# Revit family: Shower-Showerhead_Handshower_Set-KOHLER-Deluxe-K-26914_1
name_source: partatom
category: Plumbing Fixtures
units: mm (PartAtom-declared; Revit-internal decimal feet)

## family parameters
Cut with Voids When Loaded = No
Host = Face
Maintain Annotation Orientation = No
OmniClass Number = 23.31.17.00
OmniClass Title = Showers
Part Type = Normal
Room Calculation Point = No
Round Connector Dimension = Use Diameter
Shared = No

## types (6) — shared parameters
ADA Compliant = No
Assembly Code = D2010700
CW Connection = No
Cold Water Inlet = Cold Water Inlet
Date Modified = 06/23/2022
Default Elevation = 42"
Drain Included = No
HW Connection = Yes
Height = 24 1/4"
Hot Water Inlet = Tempered Water Inlet1
Length = 14 5/8"
Manufacturer = Kohler Co.
Master Format 2014 = 22 42 23
Master Format 2014 Name = Residential Showers
Material = Premium Metal Construction
Pressure = 80.00 psi
Product Documentation Link = https://www.us.kohler.com
Product Name = Deluxe
Product Page URL = http://www.us.kohler.com
Tempered Water Inlet2 = Tempered Water Inlet2
URL = https://www.us.kohler.com
Vent Connection = No
Waste Connection = No
Waste Water Outlet = Waste Water Outlet
WaterSense Certified = No
Width = 7 7/8"

## per-type parameters (varying)
| type | Description | Finish | Flow Rate | Model | Secondary Material | Type |
| 1.75 GPM, CP-Polished Chrome | Shower Kit 1.75 GPM | Kohler-Metal-CP-Polished_Chrome | 2 GPM | K-26914-G-CP | Kohler-Plastic-0-White | 1 |
| 1.75 GPM, BL-Matte Black | Shower Kit 1.75 GPM | Kohler-Metal-BL-Matte_Black | 2 GPM | K-26914-G-BL | Kohler-Plastic-58-Thunder_Grey | 2 |
| 1.75 GPM, 2MB-Vibrant Brushed Moderne Brass | Shower Kit 1.75 GPM | Kohler-Metal-2MB-Vibrant_Brushed_Moderne_Brass | 2 GPM | K-26914-G-2MB | Kohler-Plastic-0-White | 3 |
| 2.5 GPM, CP-Polished Chrome | Shower Kit 2.5 GPM | Kohler-Metal-CP-Polished_Chrome | 3 GPM | K-26914-Y-CP | Kohler-Plastic-0-White | 4 |
| 2.5 GPM, BL-Matte Black | Shower Kit 2.5 GPM | Kohler-Metal-BL-Matte_Black | 3 GPM | K-26914-Y-BL | Kohler-Plastic-58-Thunder_Grey | 5 |
| 2.5 GPM, 2MB-Vibrant Brushed Moderne Brass | Shower Kit 2.5 GPM | Kohler-Metal-2MB-Vibrant_Brushed_Moderne_Brass | 3 GPM | K-26914-Y-2MB | Kohler-Plastic-0-White | 6 |

## geometry (parser evidence)
native form markers: Sweep x7
no freeform markers — native parametric forms only
